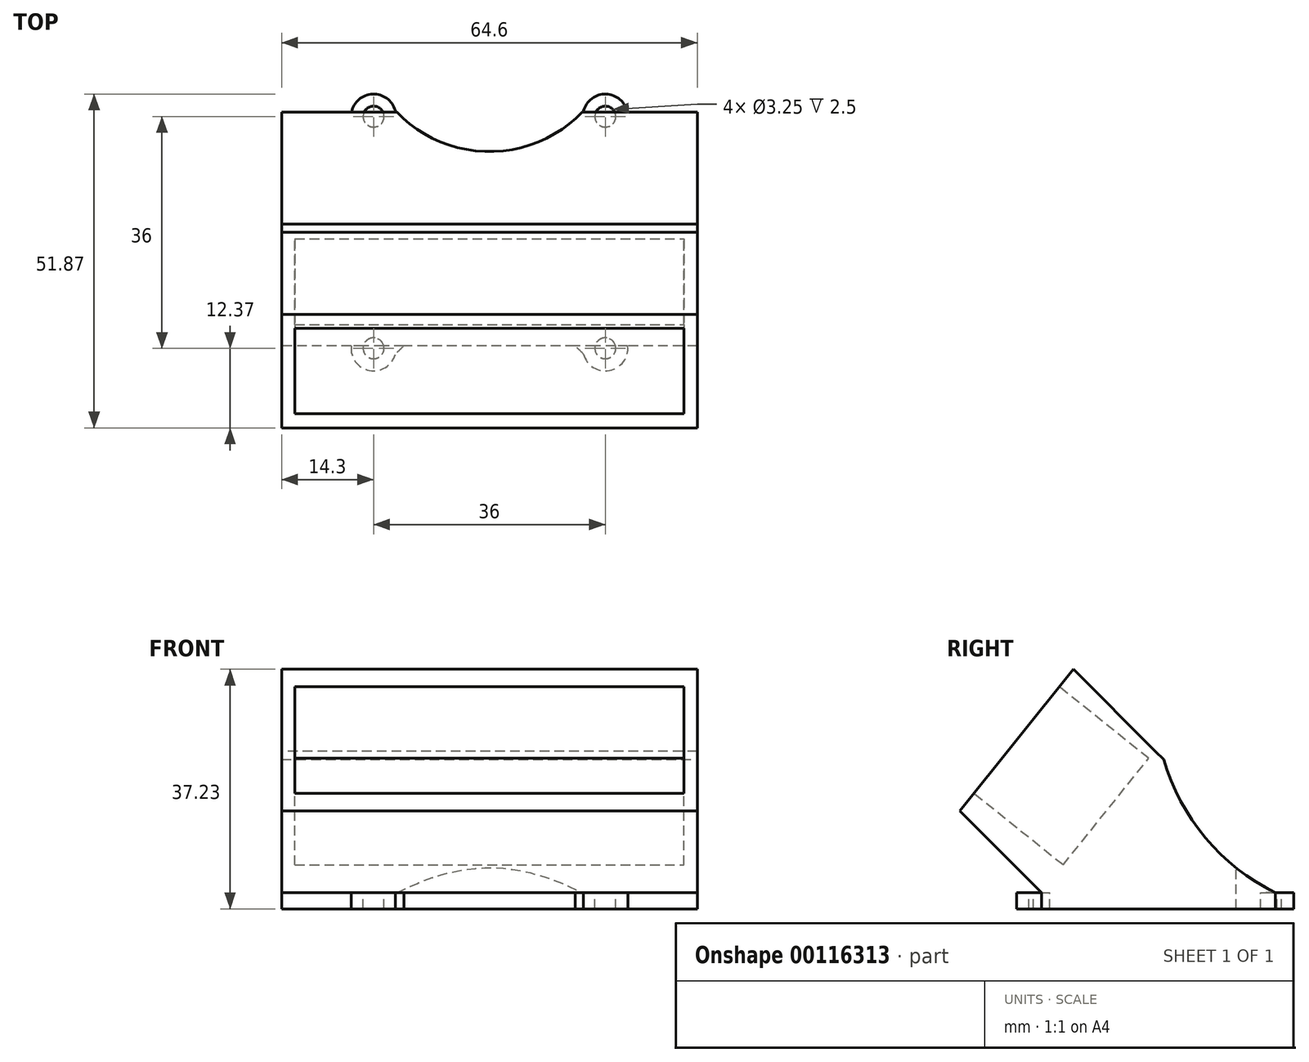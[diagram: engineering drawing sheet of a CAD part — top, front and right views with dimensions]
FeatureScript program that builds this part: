
annotation { "Feature Type Name" : "Feature", "Feature Type Description" : "" }
export const myFeature = defineFeature(function(context is Context, id is Id, definition is map)
    precondition{}
    {
        {
            var Q0;
            Q0=qCreatedBy(makeId("Top.planeOp"),FACE);
            var sketch = newSketch(context, id + "F0", { "sketchPlane" : qUnion([Q0])});
            skLineSegment(sketch, "E0.bottom", {"start": v(-18, -18) * mm, "end": v(18, -18) * mm, "construction": true});
            skLineSegment(sketch, "E0.top", {"start": v(-18, 18) * mm, "end": v(18, 18) * mm, "construction": true});
            skLineSegment(sketch, "E0.left", {"start": v(-18, -18) * mm, "end": v(-18, 18) * mm, "construction": true});
            skLineSegment(sketch, "E0.right", {"start": v(18, -18) * mm, "end": v(18, 18) * mm, "construction": true});
            skPoint(sketch, "E0.middle", {"position": v(0, 0) * mm});
            skCircle(sketch, "E1", {"center": v(18, 18) * mm, "radius": 1.63 * mm});
            skCircle(sketch, "E2.MirrorC", {"center": v(18, -18) * mm, "radius": 1.63 * mm});
            skCircle(sketch, "E3.MirrorC", {"center": v(-18, -18) * mm, "radius": 1.63 * mm});
            skCircle(sketch, "E4.MirrorC", {"center": v(-18, 18) * mm, "radius": 1.63 * mm});
            skCircle(sketch, "E5", {"center": v(-18, 18) * mm, "radius": 3.5 * mm});
            skCircle(sketch, "E6.MirrorC", {"center": v(-18, -18) * mm, "radius": 3.5 * mm});
            skCircle(sketch, "E7.MirrorC", {"center": v(18, 18) * mm, "radius": 3.5 * mm});
            skCircle(sketch, "E8.MirrorC", {"center": v(18, -18) * mm, "radius": 3.5 * mm});
            skArc(sketch, "E9", {"start": v(-14.63, 18.94) * mm, "mid": v(-0.01, 12.57) * mm, "end": v(14.62, 18.91) * mm});
            skArc(sketch, "E10.MirrorCS", {"start": v(-14.63, -18.94) * mm, "mid": v(-0.01, -12.57) * mm, "end": v(14.62, -18.91) * mm});
            skArc(sketch, "E11", {"start": v(-18.78, -14.59) * mm, "mid": v(-12.5, 0.03) * mm, "end": v(-18.87, 14.6) * mm});
            skArc(sketch, "E12.MirrorCS", {"start": v(18.78, -14.59) * mm, "mid": v(12.5, 0.03) * mm, "end": v(18.87, 14.6) * mm});
            skSolve(sketch);
        }
        {
            var Q0;
            Q0=qCreatedBy(makeId("Right.planeOp"),FACE);
            var sketch = newSketch(context, id + "F1", { "sketchPlane" : qUnion([Q0])});
            skLineSegment(sketch, "E13", {"start": v(0, 0) * mm, "end": v(23, 0) * mm, "construction": true});
            skLineSegment(sketch, "E14", {"start": v(10.63, 12.37) * mm, "end": v(15.74, 17.49) * mm, "construction": true});
            skPoint(sketch, "E15.orphan", {"position": v(-1.75, 24.75) * mm});
            skLineSegment(sketch, "E16.0", {"start": v(-17.64, 0) * mm, "end": v(-30.37, 12.73) * mm});
            skLineSegment(sketch, "E17", {"start": v(23, 0) * mm, "end": v(-17.64, 0) * mm});
            skLineSegment(sketch, "E18", {"start": v(0, 22) * mm, "end": v(23, 0) * mm});
            skLineSegment(sketch, "E19", {"start": v(0, 22) * mm, "end": v(-12.73, 34.73) * mm});
            skLineSegment(sketch, "E20", {"start": v(-30.37, 12.73) * mm, "end": v(-12.73, 34.73) * mm});
            skSolve(sketch);
        }
        {
            var Q0;
            Q0=makeQuery(id+"F1.imprint","IMPRINT",FACE,{"disambiguationData":[TD([[makeQuery(id+"F1.imprint","IMPRINT",EDGE,{"derivedFrom":sQuery(id+"F1.wireOp",EDGE,"E16.0")}),-1.0]])]});
            extrude(context, id + "F2", {"entities" : qUnion([Q0]), "depth" : 32.3 * mm});
        }
        {
            var Q0;
            Q0=makeQuery(id+"F2.opExtrude","CAP_FACE",FACE,{"disambiguationData":[OSD([sQuery(id+"F1.wireOp",EDGE,"E16.0"),sQuery(id+"F1.wireOp",EDGE,"E17"),sQuery(id+"F1.wireOp",EDGE,"E18"),sQuery(id+"F1.wireOp",EDGE,"E19"),sQuery(id+"F1.wireOp",EDGE,"E20")])],"isStart":true});
            extrude(context, id + "F3", {"entities" : qUnion([Q0]), "operationType" : NewBodyOperationType.ADD, "depth" : 32.3 * mm});
        }
        {
            var Q0;
            {var subQ0=sQuery(id+"F1.wireOp",EDGE,"E20");Q0=makeQuery(id+"F3.boolean.opBoolean","MERGE",FACE,{"derivedFrom":[makeQuery(id+"F2.opExtrude","SWEPT_FACE",FACE,{"disambiguationData":[OSD([subQ0])]}),makeQuery(id+"F3.opExtrude","SWEPT_FACE",FACE,{"disambiguationData":[OSD([subQ0])]})]});}
            var sketch = newSketch(context, id + "F4", { "sketchPlane" : qUnion([Q0])});
            skLineSegment(sketch, "E21", {"start": v(0, 19.13) * mm, "end": v(0, -9.06) * mm, "construction": true});
            skLineSegment(sketch, "E22.bottom", {"start": v(-30.22, -5.6) * mm, "end": v(30.23, -5.6) * mm});
            skLineSegment(sketch, "E22.top", {"start": v(-30.23, 15.66) * mm, "end": v(30.23, 15.66) * mm});
            skLineSegment(sketch, "E22.left", {"start": v(-30.22, -5.6) * mm, "end": v(-30.23, 15.66) * mm});
            skLineSegment(sketch, "E22.right", {"start": v(30.23, -5.6) * mm, "end": v(30.23, 15.66) * mm});
            skPoint(sketch, "E22.middle", {"position": v(0, 5.03) * mm});
            skSolve(sketch);
        }
        {
            var Q0;
            Q0=makeQuery(id+"F4.imprint","IMPRINT",FACE,{"disambiguationData":[TD([[makeQuery(id+"F4.imprint","IMPRINT",EDGE,{"derivedFrom":sQuery(id+"F4.wireOp",EDGE,"E22.bottom")}),1.0]])]});
            extrude(context, id + "F5", {"entities" : qUnion([Q0]), "operationType" : NewBodyOperationType.REMOVE, "oppositeDirection" : true, "depth" : 17.8 * mm});
        }
        {
            var Q0;
            Q0=makeQuery(id+"F2.opExtrude","CAP_FACE",FACE,{"disambiguationData":[OSD([sQuery(id+"F1.wireOp",EDGE,"E16.0"),sQuery(id+"F1.wireOp",EDGE,"E17"),sQuery(id+"F1.wireOp",EDGE,"E18"),sQuery(id+"F1.wireOp",EDGE,"E19"),sQuery(id+"F1.wireOp",EDGE,"E20")])],"isStart":false});
            var sketch = newSketch(context, id + "F6", { "sketchPlane" : qUnion([Q0])});
            skArc(sketch, "E23", {"start": v(1.32, 20.74) * mm, "mid": v(7.81, 8.54) * mm, "end": v(18.68, 0) * mm});
            skSolve(sketch);
        }
        {
            var Q0;
            Q0 = qSketchRegion(id + "F0", true);
            extrude(context, id + "F7", {"entities" : qUnion([Q0]), "operationType" : NewBodyOperationType.ADD, "oppositeDirection" : true, "depth" : 2.5 * mm});
        }
        {
            var Q0;
            {var subQ0=sQuery(id+"F6.wireOp",EDGE,"E23");Q0=makeQuery(id+"F6.imprint","IMPRINT",FACE,{"disambiguationData":[TD([[makeQuery(id+"F6.imprint","IMPRINT",EDGE,{"derivedFrom":subQ0}),1.0]])]});}
            extrude(context, id + "F8", {"entities" : qUnion([Q0]), "operationType" : NewBodyOperationType.REMOVE, "oppositeDirection" : true, "depth" : 125 * mm});
        }
        {
            var Q0;
            {var subQ0=sQuery(id+"F0.wireOp",EDGE,"E9");var subQ1=makeQuery(id+"F7.opExtrude","SWEPT_FACE",FACE,{"disambiguationData":[OSD([subQ0])]});var subQ2=sQuery(id+"F1.wireOp",EDGE,"E17");var subQ9=sQuery(id+"F1.wireOp",EDGE,"E18");Q0=makeQuery(id+"F8.boolean.opBoolean","SPLIT",FACE,{"disambiguationData":[TD([subQ1])],"derivedFrom":makeQuery(id+"F7.boolean.opBoolean","SPLIT",FACE,{"disambiguationData":[TD([makeQuery(id+"F2.opExtrude","SWEPT_FACE",FACE,{"disambiguationData":[OSD([subQ9])]})])],"derivedFrom":makeQuery(id+"F3.boolean.opBoolean","MERGE",FACE,{"derivedFrom":[makeQuery(id+"F2.opExtrude","SWEPT_FACE",FACE,{"disambiguationData":[OSD([subQ2])]}),makeQuery(id+"F3.opExtrude","SWEPT_FACE",FACE,{"disambiguationData":[OSD([subQ2])]})]})})});}
            extrude(context, id + "F9", {"entities" : qUnion([Q0]), "operationType" : NewBodyOperationType.REMOVE, "oppositeDirection" : true, "depth" : 25 * mm});
        }
        {
            var Q0;
            {var subQ2=sQuery(id+"F1.wireOp",EDGE,"E17");var subQ7=sQuery(id+"F0.wireOp",EDGE,"E7.MirrorC");var subQ13=sQuery(id+"F1.wireOp",EDGE,"E18");var subQ17=makeQuery(id+"F7.opExtrude","SWEPT_FACE",FACE,{"disambiguationData":[OSD([subQ7])]});Q0=makeQuery(id+"F8.boolean.opBoolean","SPLIT",FACE,{"disambiguationData":[TD([subQ17])],"derivedFrom":makeQuery(id+"F7.boolean.opBoolean","SPLIT",FACE,{"disambiguationData":[TD([makeQuery(id+"F2.opExtrude","SWEPT_FACE",FACE,{"disambiguationData":[OSD([subQ13])]})])],"derivedFrom":makeQuery(id+"F3.boolean.opBoolean","MERGE",FACE,{"derivedFrom":[makeQuery(id+"F2.opExtrude","SWEPT_FACE",FACE,{"disambiguationData":[OSD([subQ2])]}),makeQuery(id+"F3.opExtrude","SWEPT_FACE",FACE,{"disambiguationData":[OSD([subQ2])]})]})})});}
            var Q1;
            {var subQ6=sQuery(id+"F0.wireOp",EDGE,"E5");var subQ10=sQuery(id+"F1.wireOp",EDGE,"E18");var subQ11=sQuery(id+"F1.wireOp",EDGE,"E17");var subQ16=makeQuery(id+"F7.opExtrude","SWEPT_FACE",FACE,{"disambiguationData":[OSD([subQ6])]});Q1=makeQuery(id+"F8.boolean.opBoolean","SPLIT",FACE,{"disambiguationData":[TD([subQ16])],"derivedFrom":makeQuery(id+"F7.boolean.opBoolean","SPLIT",FACE,{"disambiguationData":[TD([makeQuery(id+"F2.opExtrude","SWEPT_FACE",FACE,{"disambiguationData":[OSD([subQ10])]})])],"derivedFrom":makeQuery(id+"F3.boolean.opBoolean","MERGE",FACE,{"derivedFrom":[makeQuery(id+"F2.opExtrude","SWEPT_FACE",FACE,{"disambiguationData":[OSD([subQ11])]}),makeQuery(id+"F3.opExtrude","SWEPT_FACE",FACE,{"disambiguationData":[OSD([subQ11])]})]})})});}
            var Q2;
            {var subQ1=sQuery(id+"F0.wireOp",EDGE,"E10.MirrorCS");var subQ2=sQuery(id+"F1.wireOp",EDGE,"E17");Q2=makeQuery(id+"F7.boolean.opBoolean","SPLIT",FACE,{"disambiguationData":[TD([makeQuery(id+"F7.opExtrude","SWEPT_FACE",FACE,{"disambiguationData":[OSD([subQ1])]})])],"derivedFrom":makeQuery(id+"F3.boolean.opBoolean","MERGE",FACE,{"derivedFrom":[makeQuery(id+"F2.opExtrude","SWEPT_FACE",FACE,{"disambiguationData":[OSD([subQ2])]}),makeQuery(id+"F3.opExtrude","SWEPT_FACE",FACE,{"disambiguationData":[OSD([subQ2])]})]})});}
            var Q3;
            Q3=makeQuery(id+"F7.opExtrude","CAP_FACE",FACE,{"disambiguationData":[OSD([sQuery(id+"F0.wireOp",EDGE,"E1"),sQuery(id+"F0.wireOp",EDGE,"E2.MirrorC"),sQuery(id+"F0.wireOp",EDGE,"E3.MirrorC"),sQuery(id+"F0.wireOp",EDGE,"E4.MirrorC"),sQuery(id+"F0.wireOp",EDGE,"E5"),sQuery(id+"F0.wireOp",EDGE,"E6.MirrorC"),sQuery(id+"F0.wireOp",EDGE,"E7.MirrorC"),sQuery(id+"F0.wireOp",EDGE,"E8.MirrorC"),sQuery(id+"F0.wireOp",EDGE,"E9"),sQuery(id+"F0.wireOp",EDGE,"E10.MirrorCS"),sQuery(id+"F0.wireOp",EDGE,"E11"),sQuery(id+"F0.wireOp",EDGE,"E12.MirrorCS")])],"isStart":false});
            extrude(context, id + "F10", {"entities" : qUnion([Q0, Q1, Q2]), "operationType" : NewBodyOperationType.ADD, "endBound" : BoundingType.UP_TO_SURFACE, "endBoundEntityFace" : qUnion([Q3]), "depth" : 25 * mm});
        }
    });
